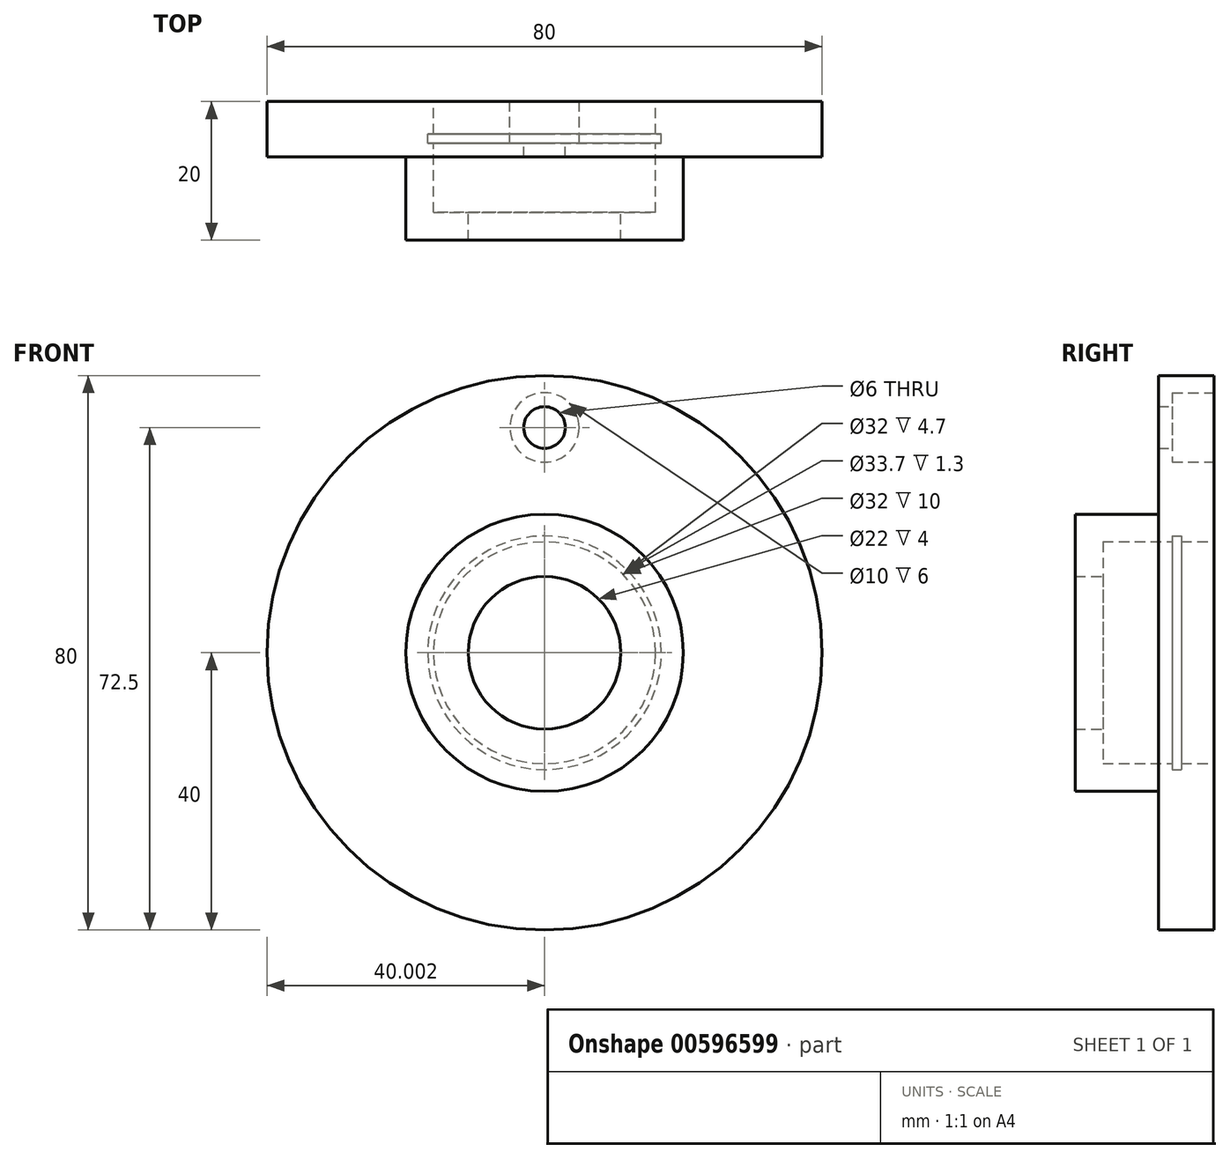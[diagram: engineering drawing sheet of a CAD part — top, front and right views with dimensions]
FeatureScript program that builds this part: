
annotation { "Feature Type Name" : "Feature", "Feature Type Description" : "" }
export const myFeature = defineFeature(function(context is Context, id is Id, definition is map)
    precondition{}
    {
        {
            var Q0;
            Q0=qCreatedBy(makeId("Top.planeOp"),FACE);
            var sketch = newSketch(context, id + "F0", { "sketchPlane" : qUnion([Q0])});
            skLineSegment(sketch, "E0", {"start": v(47.48, 2.87) * mm, "end": v(47.48, -5.13) * mm});
            skLineSegment(sketch, "E1", {"start": v(7.48, 5.58) * mm, "end": v(7.48, -19.31) * mm});
            skLineSegment(sketch, "E2", {"start": v(27.48, -5.13) * mm, "end": v(27.48, -17.13) * mm});
            skLineSegment(sketch, "E3", {"start": v(23.48, 2.87) * mm, "end": v(23.48, -1.83) * mm});
            skLineSegment(sketch, "E4", {"start": v(27.48, -5.13) * mm, "end": v(47.48, -5.13) * mm});
            skLineSegment(sketch, "E5", {"start": v(23.48, -3.13) * mm, "end": v(23.48, -13.13) * mm});
            skLineSegment(sketch, "E6", {"start": v(23.48, -13.13) * mm, "end": v(18.48, -13.13) * mm});
            skLineSegment(sketch, "E7", {"start": v(18.48, -13.13) * mm, "end": v(18.48, -17.13) * mm});
            skLineSegment(sketch, "E8", {"start": v(24.33, -3.13) * mm, "end": v(23.48, -3.13) * mm});
            skLineSegment(sketch, "E9", {"start": v(24.33, -1.83) * mm, "end": v(23.48, -1.83) * mm});
            skLineSegment(sketch, "E10", {"start": v(24.33, -1.83) * mm, "end": v(24.33, -3.13) * mm});
            skLineSegment(sketch, "E11.trimOffspring", {"start": v(23.48, 2.87) * mm, "end": v(47.48, 2.87) * mm});
            skLineSegment(sketch, "E12.trimOffspring", {"start": v(18.48, -13.13) * mm, "end": v(23.48, -13.13) * mm});
            skLineSegment(sketch, "E13.trimOffspring", {"start": v(18.48, -17.13) * mm, "end": v(27.48, -17.13) * mm});
            skSolve(sketch);
        }
        {
            var Q0;
            Q0=makeQuery(id+"F0.imprint","IMPRINT",FACE,{"disambiguationData":[TD([[makeQuery(id+"F0.imprint","IMPRINT",EDGE,{"derivedFrom":sQuery(id+"F0.wireOp",EDGE,"E0")}),-1.0]])]});
            var Q1;
            Q1=sQuery(id+"F0.wireOp",EDGE,"E1");
            revolve(context, id + "F1", {"entities" : qUnion([Q0]), "axis" : qUnion([Q1]), "revolveType" : RevolveType.FULL});
        }
        {
            var Q0;
            Q0=makeQuery(id+"F1.opRevolve","SWEPT_FACE",FACE,{"disambiguationData":[OSD([sQuery(id+"F0.wireOp",EDGE,"E11.trimOffspring")])]});
            var sketch = newSketch(context, id + "F2", { "sketchPlane" : qUnion([Q0])});
            skCircle(sketch, "E14", {"center": v(-7.48, 0) * mm, "radius": 32.5 * mm, "construction": true});
            skLineSegment(sketch, "E15", {"start": v(-7.48, 0) * mm, "end": v(-7.48, 32.5) * mm, "construction": true});
            skPoint(sketch, "E16", {"position": v(-7.48, 32.5) * mm});
            skSolve(sketch);
        }
        {
            var Q0;
            Q0=sQuery(id+"F2.wireOp",VERTEX,"E16");
            var Q1;
            Q1=makeQuery(id+"F1.opRevolve","SWEPT_BODY",BODY,{"disambiguationData":[OSD([sQuery(id+"F0.wireOp",EDGE,"E0"),sQuery(id+"F0.wireOp",EDGE,"E2"),sQuery(id+"F0.wireOp",EDGE,"E3"),sQuery(id+"F0.wireOp",EDGE,"E4"),sQuery(id+"F0.wireOp",EDGE,"E7"),sQuery(id+"F0.wireOp",EDGE,"E5"),sQuery(id+"F0.wireOp",EDGE,"E8"),sQuery(id+"F0.wireOp",EDGE,"E9"),sQuery(id+"F0.wireOp",EDGE,"E10"),sQuery(id+"F0.wireOp",EDGE,"E11.trimOffspring"),sQuery(id+"F0.wireOp",EDGE,"E12.trimOffspring"),sQuery(id+"F0.wireOp",EDGE,"E13.trimOffspring")])]});
            hole(context, id + "F3", {"style" : HoleStyle.SIMPLE, "endStyle" : HoleEndStyle.THROUGH, "holeDiameter" : 6 * mm, "majorDiameter" : 5 * mm, "isTappedThrough" : true, "tappedDepth" : 12 * mm, "tapClearance" : 3, "startFromSketch" : true, "locations" : qUnion([Q0]), "scope" : qUnion([Q1])});
        }
        {
            var Q0;
            Q0=makeQuery(id+"F1.opRevolve","SWEPT_FACE",FACE,{"disambiguationData":[OSD([sQuery(id+"F0.wireOp",EDGE,"E11.trimOffspring")])]});
            var sketch = newSketch(context, id + "F4", { "sketchPlane" : qUnion([Q0])});
            skCircle(sketch, "E17", {"center": v(-7.48, 32.5) * mm, "radius": 5 * mm});
            skSolve(sketch);
        }
        {
            var Q0;
            Q0=makeQuery(id+"F4.imprint","IMPRINT",FACE,{"disambiguationData":[TD([[makeQuery(id+"F4.imprint","IMPRINT",EDGE,{"derivedFrom":sQuery(id+"F4.wireOp",EDGE,"E17")}),1.0]])]});
            extrude(context, id + "F5", {"entities" : qUnion([Q0]), "operationType" : NewBodyOperationType.REMOVE, "oppositeDirection" : true, "depth" : 6 * mm, "offsetDistance" : 25 * mm});
        }
    });
